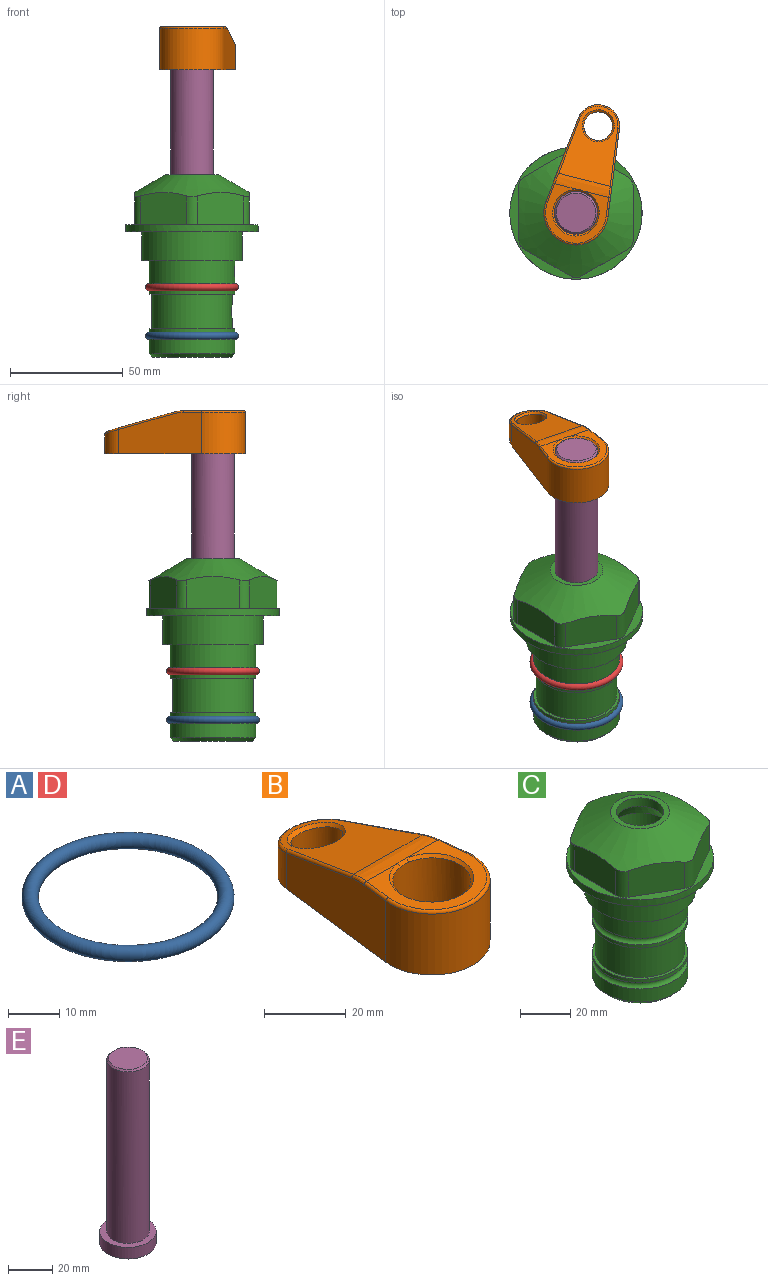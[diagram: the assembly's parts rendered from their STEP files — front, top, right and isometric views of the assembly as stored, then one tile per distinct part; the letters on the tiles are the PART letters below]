
ASSEMBLY  parts=5 mates=4
PART A: 1 faces, bbox 44.7x44.7x3.2 mm
  f0: torus R=19.05mm, axis (0,0,1), area 1193.9mm2
PART B: 31 faces, bbox 31.7x65.5x19.8 mm
  f0: plane 39.12x18.26mm, normal (0.99,0.12,0), area 612.2mm2, adj f1,f4,f7,f11,f13,f15
  f1: cylinder r=9.53mm len=18.91mm, axis (0,0,-1), area 296.1mm2, adj f0,f2,f7,f17
  f2: plane 39.12x18.26mm, normal (-0.99,0.12,0), area 612.2mm2, adj f1,f4,f7,f12,f14,f16
  f3: cylinder r=6.35mm len=12.7mm, axis (0,0,-1), area 362.4mm2, adj f7,f18
  f4: cylinder r=14.29mm len=28.58mm, axis (0,0,-1), area 882.2mm2, adj f0,f2,f7,f10
  f5: cylinder r=9.53mm len=19.05mm, axis (0,0,-1), area 1092.6mm2, adj f7,f19,f20
  f6: plane 26.99x23.69mm, normal (0,0,1), area 216.2mm2, adj f9,f10,f11,f12,f19
  f7: plane 63.5x28.58mm, normal (0,0,-1), area 661.8mm2, adj f0,f1,f2,f3,f4,f5,f22,f23
  f8: plane 33.52x23.6mm, normal (0,0.26,0.97), area 486mm2, adj f9,f15,f16,f17,f18
  f9: cylinder r=19.05mm len=24.72mm, axis (1,0,0), area 120.4mm2, adj f6,f8,f13,f14,f20
  f10: torus R=13.49mm, axis (0,0,1), area 59mm2, adj f4,f6,f11,f12
  f11: cylinder r=0.79mm len=8.67mm, axis (0.12,-0.99,0), area 10.8mm2, adj f0,f6,f10,f13
  f12: cylinder r=0.79mm len=8.67mm, axis (0.12,0.99,0), area 10.8mm2, adj f2,f6,f10,f14
  f13: bspline ~4.95x1.42mm, area 6.1mm2, adj f0,f9,f11,f15
  f14: bspline ~4.95x1.42mm, area 6.1mm2, adj f2,f9,f12,f16
  f15: cylinder r=0.79mm len=25.95mm, axis (0.12,-0.96,0.26), area 32.9mm2, adj f0,f8,f13,f17
  f16: cylinder r=0.79mm len=25.95mm, axis (0.12,0.96,-0.26), area 32.9mm2, adj f2,f8,f14,f17
  f17: bspline ~18.91x8.38mm, area 30mm2, adj f1,f8,f15,f16
  f18: bspline ~14.29x14.29mm, area 48.3mm2, adj f3,f8
  f19: cone r=9.53mm half-angle=45deg, axis (0,0,1), area 66.5mm2, adj f5,f6,f20
  f20: bspline ~3.22x0.96mm, area 3.5mm2, adj f5,f9,f19
  f21: plane 2.75x2.72mm, normal (0,0,-1), area 2.9mm2, adj f23,f25,f28
  f22: plane 23.05x15.88mm, normal (-0.99,-0.12,0), area 323.6mm2, adj f7,f25,f26,f27,f28,f29
  f23: plane 23.05x15.88mm, normal (0.99,-0.12,0), area 323.6mm2, adj f7,f21,f25,f27,f28,f30
  f24: cylinder r=9.53mm len=10.69mm, axis (0,0,-1), area 114.7mm2, adj f7,f27,f29,f30
  f25: cylinder r=12.7mm len=20.59mm, axis (0,0,-1), area 381.1mm2, adj f7,f21,f22,f23,f26,f28
  f26: plane 2.75x2.72mm, normal (0,0,-1), area 2.9mm2, adj f22,f25,f28
  f27: plane 19.72x18.37mm, normal (0,-0.26,-0.97), area 291.8mm2, adj f22,f23,f24,f28,f29,f30
  f28: cylinder r=15.88mm len=19.92mm, axis (1,0,0), area 54.8mm2, adj f21,f22,f23,f25,f26,f27
  f29: cylinder r=1.59mm len=11mm, axis (0,0,-1), area 34.7mm2, adj f7,f22,f24,f27
  f30: cylinder r=1.59mm len=11mm, axis (0,0,-1), area 34.7mm2, adj f7,f23,f24,f27
PART C: 36 faces, bbox 58.7x58.7x81 mm
  f0: cylinder r=17.78mm len=35.56mm, axis (0,0,1), area 1670.8mm2, adj f23,f24,f31
  f1: cylinder r=19.05mm len=38.1mm, axis (0,0,1), area 1191.9mm2, adj f26,f27,f30
  f2: plane 58.66x58.66mm, normal (0,0,-1), area 1150.6mm2, adj f3,f28
  f3: cylinder r=29.33mm len=58.66mm, axis (0,0,-1), area 585.1mm2, adj f2,f4
  f4: plane 58.66x58.66mm, normal (0,0,1), area 475.9mm2, adj f3,f5,f6,f7,f8,f9,f10,f11
  f5: plane 20.32x14.34mm, normal (-0.5,0.87,0), area 324.4mm2, adj f4,f15,f16,f17
  f6: plane 20.32x14.34mm, normal (0.5,0.87,0), area 324.4mm2, adj f4,f14,f15,f17
  f7: plane 23.48x14.34mm, normal (1,0,0), area 324.4mm2, adj f4,f13,f14,f17
  f8: plane 20.32x14.34mm, normal (0.5,-0.87,0), area 324.4mm2, adj f4,f12,f13,f17
  f9: plane 20.32x14.34mm, normal (-0.5,-0.87,0), area 324.4mm2, adj f4,f11,f12,f17
  f10: plane 23.48x14.34mm, normal (-1,0,0), area 324.4mm2, adj f4,f11,f16,f17
  f11: cylinder r=5.08mm len=12.85mm, axis (0,0,-1), area 67.2mm2, adj f4,f9,f10,f17
  f12: cylinder r=5.08mm len=12.85mm, axis (0,0,-1), area 67.2mm2, adj f4,f8,f9,f17
  f13: cylinder r=5.08mm len=12.85mm, axis (0,0,-1), area 67.2mm2, adj f4,f7,f8,f17
  f14: cylinder r=5.08mm len=12.85mm, axis (0,0,-1), area 67.2mm2, adj f4,f6,f7,f17
  f15: cylinder r=5.08mm len=12.85mm, axis (0,0,-1), area 67.2mm2, adj f4,f5,f6,f17
  f16: cylinder r=5.08mm len=12.85mm, axis (0,0,-1), area 67.2mm2, adj f4,f5,f10,f17
  f17: cone r=11.73mm half-angle=60deg, axis (0,0,-1), area 2071.8mm2, adj f5,f6,f7,f8,f9,f10,f11,f12
  f18: plane 23.46x23.46mm, normal (0,0,1), area 147.4mm2, adj f17,f35
  f19: plane 34.93x34.93mm, normal (0,0,-1), area 958mm2, adj f29
  f20: cylinder r=19.05mm len=38.1mm, axis (0,0,1), area 760.1mm2, adj f21,f29
  f21: torus R=19.05mm, axis (0,0,1), area 565.3mm2, adj f20,f22
  f22: cylinder r=19.05mm len=38.1mm, axis (0,0,1), area 190mm2, adj f21,f23
  f23: plane 38.1x38.1mm, normal (0,0,1), area 146.9mm2, adj f0,f22
  f24: plane 38.1x38.1mm, normal (0,0,-1), area 146.9mm2, adj f0,f25
  f25: cylinder r=19.05mm len=38.1mm, axis (0,0,1), area 190mm2, adj f24,f26
  f26: torus R=19.05mm, axis (0,0,1), area 565.3mm2, adj f1,f25
  f27: plane 44.45x44.45mm, normal (0,0,-1), area 411.7mm2, adj f1,f28
  f28: cylinder r=22.23mm len=44.45mm, axis (0,0,1), area 1773.5mm2, adj f2,f27
  f29: cone r=19.05mm half-angle=45deg, axis (0,0,1), area 257.5mm2, adj f19,f20
  f30: cylinder r=3.17mm len=6.75mm, axis (-1,0,0), area 128mm2, adj f1,f33
  f31: cylinder r=3.17mm len=6.35mm, axis (-1,0,0), area 102.5mm2, adj f0,f33
  f32: plane 25.4x25.4mm, normal (0,0,1), area 506.7mm2, adj f33
  f33: cylinder r=12.7mm len=66.42mm, axis (0,0,-1), area 5236.2mm2, adj f30,f31,f32,f34
  f34: cone r=9.53mm half-angle=30deg, axis (0,0,-1), area 443.4mm2, adj f33,f35
  f35: cylinder r=9.53mm len=19.05mm, axis (0,0,-1), area 240.9mm2, adj f18,f34
PART D: same geometry as A
PART E: 6 faces, bbox 25.4x25.4x101.6 mm
  f0: plane 17.46x17.46mm, normal (0,0,1), area 239.5mm2, adj f5
  f1: plane 25.4x25.4mm, normal (0,0,-1), area 506.7mm2, adj f2
  f2: cylinder r=12.7mm len=25.4mm, axis (0,0,1), area 506.7mm2, adj f1,f3
  f3: plane 25.4x25.4mm, normal (0,0,1), area 221.7mm2, adj f2,f4
  f4: cylinder r=9.53mm len=94.46mm, axis (0,0,1), area 5653mm2, adj f3,f5
  f5: cone r=8.73mm half-angle=45deg, axis (0,0,-1), area 64.4mm2, adj f0,f4
PLACE A t=(0,0,-21.59)mm
PLACE B rot(axis=(0,0,-1),14.4deg) t=(0,0,27.55)mm
PLACE C at identity fixed
PLACE D at identity
PLACE E rot(axis=(0,0,-1),14.4deg) t=(0,0,27.55)mm
MATE fastened C.f0 <-> D.f0  axis (0,0,1) through (0,0,-24.51)mm
MATE fastened C.f0 <-> A.f0  axis (0,0,1) through (0,0,-46.1)mm
MATE cylindrical E.f2 <-> C.f0  axis (0,0,-1) through (0,0,-10.55)mm
MATE fastened B.f4 <-> E.f2  axis (0,0,1) through (0,0,91.05)mm
